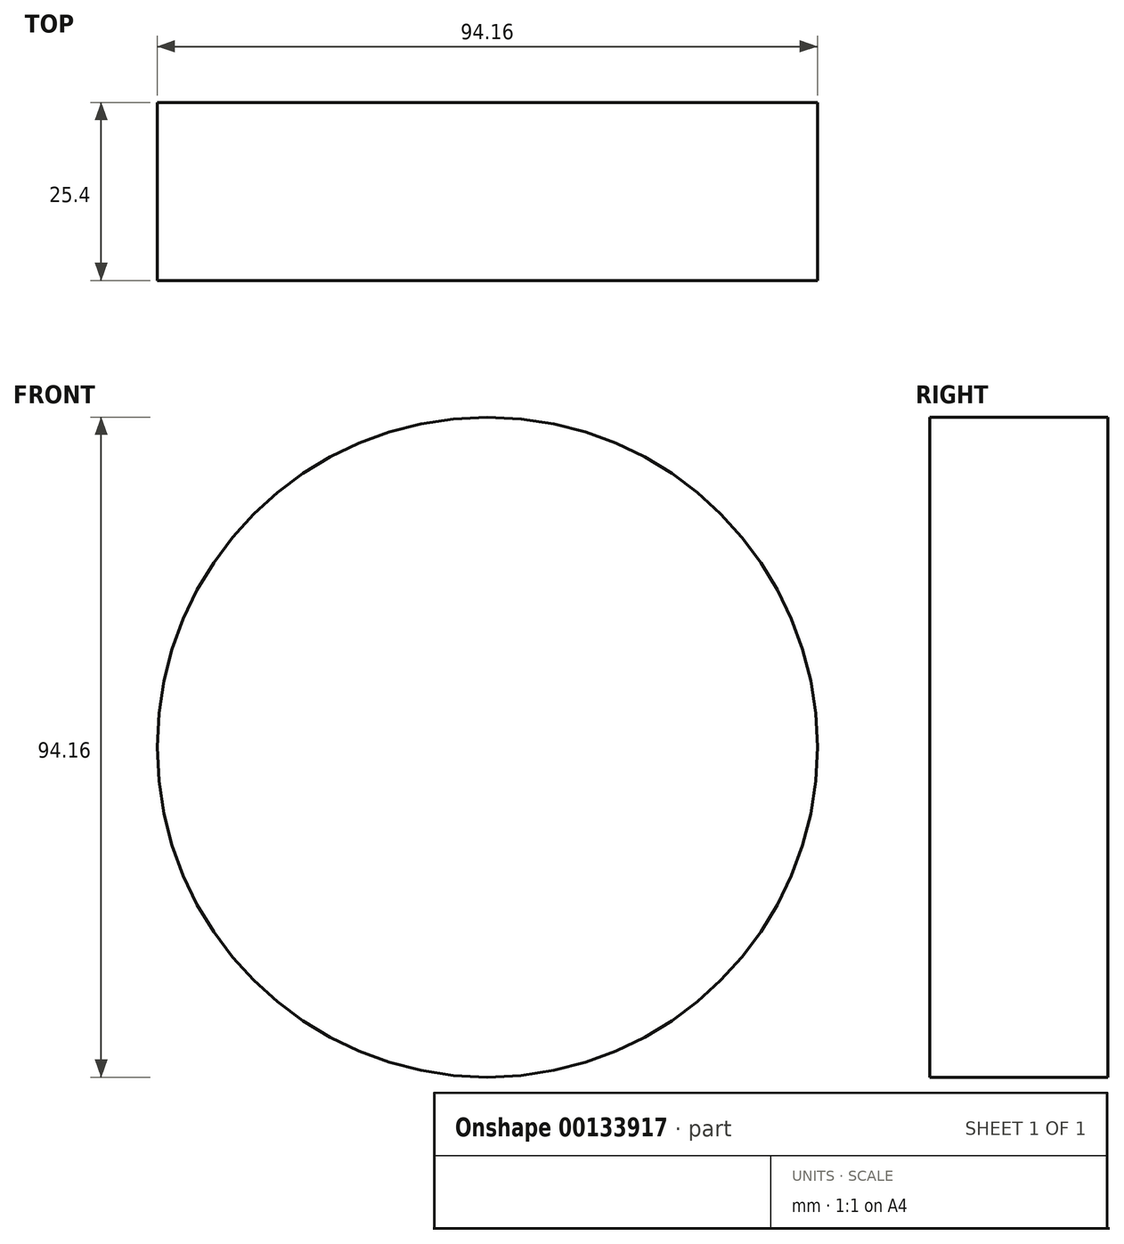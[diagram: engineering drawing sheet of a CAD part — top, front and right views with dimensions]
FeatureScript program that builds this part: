
annotation { "Feature Type Name" : "Feature", "Feature Type Description" : "" }
export const myFeature = defineFeature(function(context is Context, id is Id, definition is map)
    precondition{}
    {
        {
            var Q0;
            Q0=qCreatedBy(makeId("Front.planeOp"),FACE);
            var sketch = newSketch(context, id + "F0", { "sketchPlane" : qUnion([Q0])});
            skCircle(sketch, "E0", {"center": v(0, 0) * mm, "radius": 47.08 * mm});
            skSolve(sketch);
        }
        {
            var Q0;
            Q0=makeQuery(id+"F0.imprint","IMPRINT",FACE,{"disambiguationData":[TD([[makeQuery(id+"F0.imprint","IMPRINT",EDGE,{"derivedFrom":sQuery(id+"F0.wireOp",EDGE,"E0")}),1.0]])]});
            var Q1;
            Q1=makeQuery(id+"F0.imprint","IMPRINT",FACE,{"disambiguationData":[TD([[makeQuery(id+"F0.imprint","IMPRINT",EDGE,{"derivedFrom":sQuery(id+"F0.wireOp",EDGE,"E0")}),1.0]])]});
            var Q2;
            Q2=sQuery(id+"F0.wireOp",EDGE,"E0");
            extrude(context, id + "F1", {"entities" : qUnion([Q0, Q1]), "surfaceEntities" : qUnion([Q2]), "depth" : 25.4 * mm});
        }
    });
